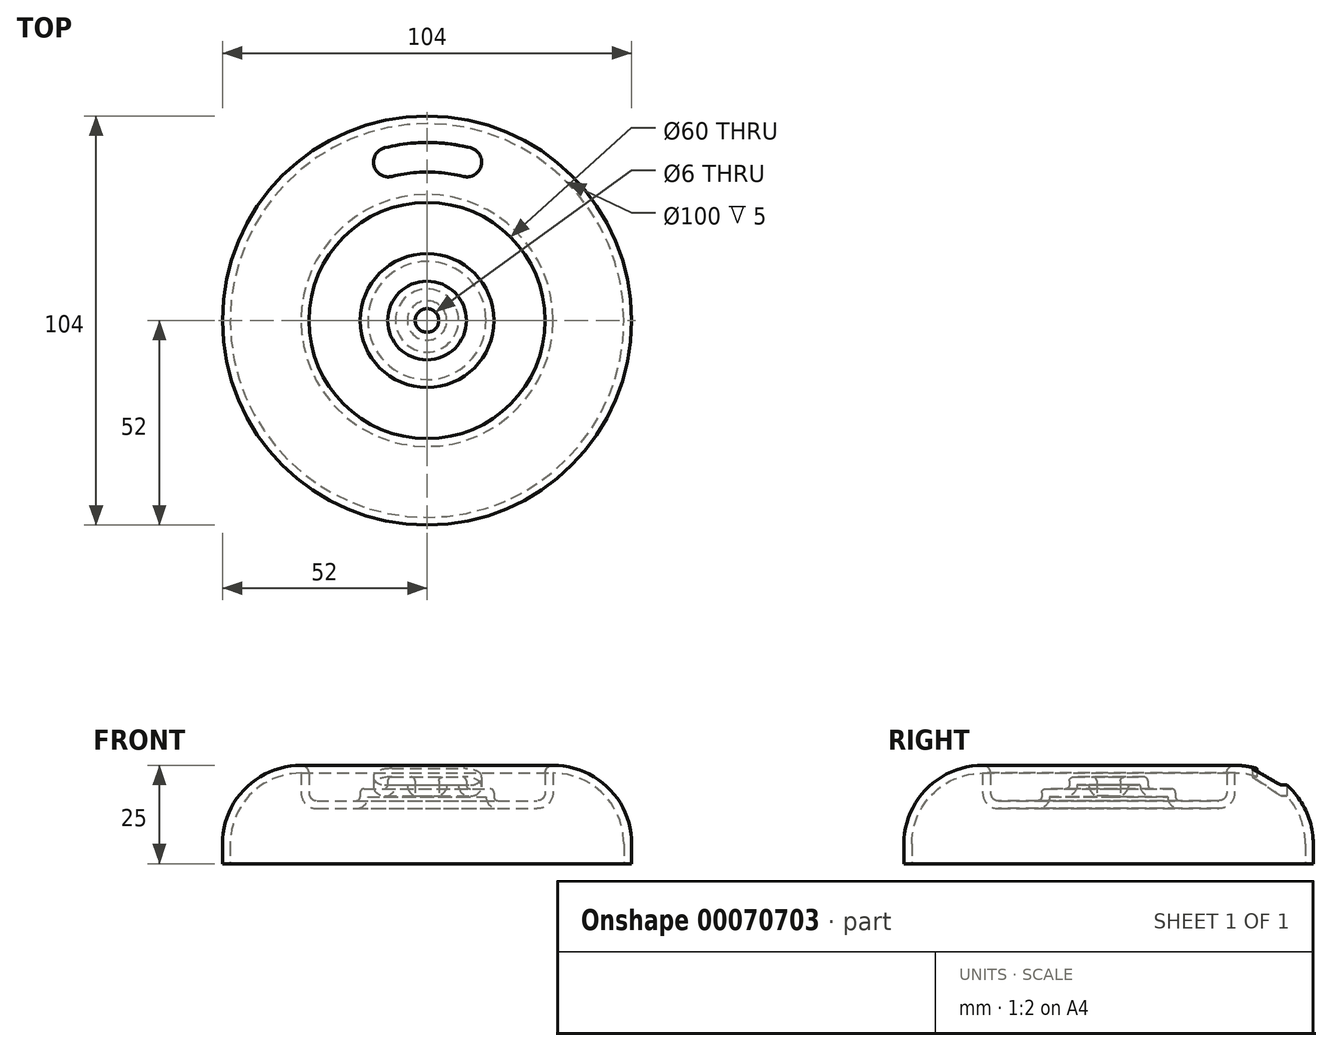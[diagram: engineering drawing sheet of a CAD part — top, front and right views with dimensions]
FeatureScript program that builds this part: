
annotation { "Feature Type Name" : "Feature", "Feature Type Description" : "" }
export const myFeature = defineFeature(function(context is Context, id is Id, definition is map)
    precondition{}
    {
        {
            var Q0;
            Q0=qCreatedBy(makeId("Front.planeOp"),FACE);
            var sketch = newSketch(context, id + "F0", { "sketchPlane" : qUnion([Q0])});
            skLineSegment(sketch, "E0", {"start": v(0, 0) * mm, "end": v(52, 0) * mm});
            skLineSegment(sketch, "E1", {"start": v(52, 0) * mm, "end": v(52, 5) * mm});
            skLineSegment(sketch, "E2", {"start": v(0, 0) * mm, "end": v(0, 19) * mm});
            skLineSegment(sketch, "E3", {"start": v(0, 19) * mm, "end": v(2, 19) * mm});
            skLineSegment(sketch, "E4", {"start": v(3, 20) * mm, "end": v(3, 21) * mm});
            skLineSegment(sketch, "E5", {"start": v(4, 22) * mm, "end": v(9, 22) * mm});
            skLineSegment(sketch, "E6", {"start": v(10, 21) * mm, "end": v(10, 20) * mm});
            skLineSegment(sketch, "E7", {"start": v(11, 19) * mm, "end": v(16, 19) * mm});
            skLineSegment(sketch, "E8", {"start": v(17, 18) * mm, "end": v(17, 17) * mm});
            skLineSegment(sketch, "E9", {"start": v(18, 16) * mm, "end": v(28, 16) * mm});
            skLineSegment(sketch, "E10", {"start": v(30, 18) * mm, "end": v(30, 23) * mm});
            skLineSegment(sketch, "E11", {"start": v(32, 25) * mm, "end": v(32, 25) * mm});
            skPoint(sketch, "E12.visualSharp", {"position": v(52, 25) * mm});
            skArc(sketch, "E12.filletArc", {"start": v(52, 5) * mm, "mid": v(46.14, 19.14) * mm, "end": v(32, 25) * mm});
            skPoint(sketch, "E13.visualSharp", {"position": v(30, 25) * mm});
            skArc(sketch, "E13.filletArc", {"start": v(32, 25) * mm, "mid": v(30.59, 24.41) * mm, "end": v(30, 23) * mm});
            skPoint(sketch, "E14.visualSharp", {"position": v(30, 16) * mm});
            skArc(sketch, "E14.filletArc", {"start": v(28, 16) * mm, "mid": v(29.41, 16.59) * mm, "end": v(30, 18) * mm});
            skPoint(sketch, "E15.visualSharp", {"position": v(17, 16) * mm});
            skArc(sketch, "E15.filletArc", {"start": v(17, 17) * mm, "mid": v(17.3, 16.3) * mm, "end": v(18, 16) * mm});
            skPoint(sketch, "E16.visualSharp", {"position": v(3, 19) * mm});
            skArc(sketch, "E16.filletArc", {"start": v(2, 19) * mm, "mid": v(2.7, 19.3) * mm, "end": v(3, 20) * mm});
            skPoint(sketch, "E17.visualSharp", {"position": v(3, 22) * mm});
            skArc(sketch, "E17.filletArc", {"start": v(4, 22) * mm, "mid": v(3.3, 21.7) * mm, "end": v(3, 21) * mm});
            skPoint(sketch, "E18.visualSharp", {"position": v(10, 22) * mm});
            skArc(sketch, "E18.filletArc", {"start": v(10, 21) * mm, "mid": v(9.7, 21.7) * mm, "end": v(9, 22) * mm});
            skPoint(sketch, "E19.visualSharp", {"position": v(10, 19) * mm});
            skArc(sketch, "E19.filletArc", {"start": v(10, 20) * mm, "mid": v(10.3, 19.3) * mm, "end": v(11, 19) * mm});
            skPoint(sketch, "E20.visualSharp", {"position": v(17, 19) * mm});
            skArc(sketch, "E20.filletArc", {"start": v(17, 18) * mm, "mid": v(16.7, 18.7) * mm, "end": v(16, 19) * mm});
            skSolve(sketch);
        }
        {
            var Q0;
            Q0=makeQuery(id+"F0.imprint","IMPRINT",FACE,{"disambiguationData":[TD([[makeQuery(id+"F0.imprint","IMPRINT",EDGE,{"derivedFrom":sQuery(id+"F0.wireOp",EDGE,"E0")}),1.0]])]});
            var Q1;
            Q1=sQuery(id+"F0.wireOp",EDGE,"E2");
            revolve(context, id + "F1", {"entities" : qUnion([Q0]), "axis" : qUnion([Q1]), "revolveType" : RevolveType.FULL});
        }
        {
            var Q0;
            Q0=qCreatedBy(makeId("Top.planeOp"),FACE);
            var sketch = newSketch(context, id + "F2", { "sketchPlane" : qUnion([Q0])});
            skCircle(sketch, "E21", {"center": v(0.14, 0.22) * mm, "radius": 41.25 * mm, "construction": true});
            skLineSegment(sketch, "E22", {"start": v(0.14, 0.22) * mm, "end": v(-9.86, 40.24) * mm, "construction": true});
            skLineSegment(sketch, "E23", {"start": v(-9.86, 40.24) * mm, "end": v(10.14, 40.24) * mm, "construction": true});
            skLineSegment(sketch, "E24", {"start": v(10.14, 40.24) * mm, "end": v(0.14, 0.22) * mm, "construction": true});
            skArc(sketch, "E25", {"start": v(-10.77, 43.88) * mm, "mid": v(-13.5, 39.34) * mm, "end": v(-8.95, 36.6) * mm});
            skArc(sketch, "E26", {"start": v(-8.95, 36.6) * mm, "mid": v(-6.22, 41.15) * mm, "end": v(-10.77, 43.88) * mm, "construction": true});
            skArc(sketch, "E27", {"start": v(11.05, 43.88) * mm, "mid": v(6.5, 41.15) * mm, "end": v(9.23, 36.6) * mm, "construction": true});
            skArc(sketch, "E28", {"start": v(9.23, 36.6) * mm, "mid": v(13.78, 39.34) * mm, "end": v(11.05, 43.88) * mm});
            skLineSegment(sketch, "E29", {"start": v(-10.77, 43.88) * mm, "end": v(-10.77, 43.88) * mm});
            skLineSegment(sketch, "E30", {"start": v(11.05, 43.88) * mm, "end": v(11.05, 43.88) * mm});
            skArc(sketch, "E31", {"start": v(-8.95, 36.6) * mm, "mid": v(0.14, -37.28) * mm, "end": v(9.23, 36.6) * mm, "construction": true});
            skArc(sketch, "E32", {"start": v(9.23, 36.6) * mm, "mid": v(0.14, 37.72) * mm, "end": v(-8.95, 36.6) * mm});
            skArc(sketch, "E33", {"start": v(-10.77, 43.88) * mm, "mid": v(0.14, -44.78) * mm, "end": v(11.05, 43.88) * mm, "construction": true});
            skArc(sketch, "E34", {"start": v(11.05, 43.88) * mm, "mid": v(0.14, 45.22) * mm, "end": v(-10.77, 43.88) * mm});
            skSolve(sketch);
        }
        {
            var Q0;
            Q0=makeQuery(id+"F1.opRevolve","SWEPT_FACE",FACE,{"disambiguationData":[OSD([sQuery(id+"F0.wireOp",EDGE,"E0")])]});
            shell(context, id + "F3", {"entities" : qUnion([Q0]), "thickness" : 2 * mm});
        }
        {
            var Q0;
            Q0=makeQuery(id+"F2.imprint","IMPRINT",FACE,{"disambiguationData":[TD([[makeQuery(id+"F2.imprint","IMPRINT",EDGE,{"derivedFrom":sQuery(id+"F2.wireOp",EDGE,"E25")}),1.0]])]});
            var Q1;
            Q1=sQuery(id+"F2.wireOp",EDGE,"E32");
            var Q2;
            Q2=sQuery(id+"F2.wireOp",EDGE,"E25");
            var Q3;
            Q3=sQuery(id+"F2.wireOp",EDGE,"E34");
            var Q4;
            Q4=sQuery(id+"F2.wireOp",EDGE,"E28");
            extrude(context, id + "F4", {"entities" : qUnion([Q0]), "operationType" : NewBodyOperationType.REMOVE, "surfaceEntities" : qUnion([Q1, Q2, Q3, Q4]), "endBound" : BoundingType.THROUGH_ALL, "depth" : 25 * mm});
        }
        {
            var Q0;
            Q0=qCreatedBy(makeId("Top.planeOp"),FACE);
            var sketch = newSketch(context, id + "F5", { "sketchPlane" : qUnion([Q0])});
            skPoint(sketch, "E35", {"position": v(0, 0) * mm});
            skSolve(sketch);
        }
        {
            var Q0;
            Q0=sQuery(id+"F5.wireOp",VERTEX,"E35");
            var Q1;
            Q1=makeQuery(id+"F1.opRevolve","SWEPT_BODY",BODY,{"disambiguationData":[OSD([sQuery(id+"F0.wireOp",EDGE,"E0"),sQuery(id+"F0.wireOp",EDGE,"E1"),sQuery(id+"F0.wireOp",EDGE,"E2"),sQuery(id+"F0.wireOp",EDGE,"E3"),sQuery(id+"F0.wireOp",EDGE,"E4"),sQuery(id+"F0.wireOp",EDGE,"E5"),sQuery(id+"F0.wireOp",EDGE,"E6"),sQuery(id+"F0.wireOp",EDGE,"E7"),sQuery(id+"F0.wireOp",EDGE,"E8"),sQuery(id+"F0.wireOp",EDGE,"E9"),sQuery(id+"F0.wireOp",EDGE,"E10"),sQuery(id+"F0.wireOp",EDGE,"E12.filletArc"),sQuery(id+"F0.wireOp",EDGE,"E13.filletArc"),sQuery(id+"F0.wireOp",EDGE,"E14.filletArc"),sQuery(id+"F0.wireOp",EDGE,"E15.filletArc"),sQuery(id+"F0.wireOp",EDGE,"E16.filletArc"),sQuery(id+"F0.wireOp",EDGE,"E17.filletArc"),sQuery(id+"F0.wireOp",EDGE,"E18.filletArc"),sQuery(id+"F0.wireOp",EDGE,"E19.filletArc"),sQuery(id+"F0.wireOp",EDGE,"E20.filletArc")])]});
            hole(context, id + "F6", {"style" : HoleStyle.SIMPLE, "holeDiameter" : 6 * mm, "endStyle" : HoleEndStyle.THROUGH, "oppositeDirection" : true, "locations" : qUnion([Q0]), "scope" : qUnion([Q1])});
        }
    });
